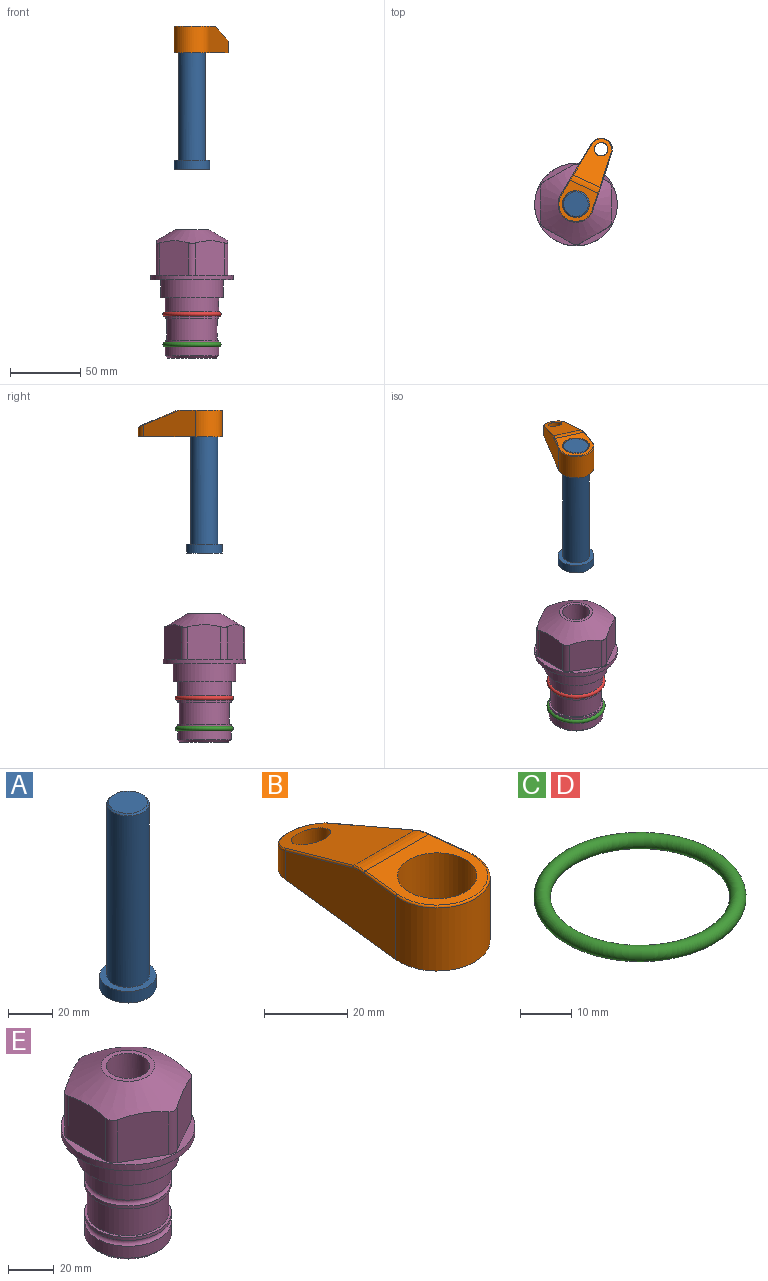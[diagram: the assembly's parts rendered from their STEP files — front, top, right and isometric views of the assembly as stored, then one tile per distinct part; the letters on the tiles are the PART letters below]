
ASSEMBLY  parts=5 mates=3
PART A: 6 faces, bbox 25.4x25.4x101.6 mm
  f0: plane 17.46x17.46mm, normal (0,0,1), area 239.5mm2, adj f5
  f1: plane 25.4x25.4mm, normal (0,0,-1), area 506.7mm2, adj f2
  f2: cylinder r=12.7mm len=25.4mm, axis (0,0,1), area 506.7mm2, adj f1,f3
  f3: plane 25.4x25.4mm, normal (0,0,1), area 221.7mm2, adj f2,f4
  f4: cylinder r=9.53mm len=94.46mm, axis (0,0,1), area 5653mm2, adj f3,f5
  f5: cone r=8.73mm half-angle=45deg, axis (0,0,-1), area 64.4mm2, adj f0,f4
PART B: 44 faces, bbox 27.5x64.5x19.1 mm
  f0: plane 2.3x0.95mm, normal (0,0,-1), area 1mm2, adj f25,f30,f34
  f1: plane 63.5x25.4mm, normal (0,0,-1), area 561.7mm2, adj f2,f3,f4,f5,f6,f7,f19,f20
  f2: cylinder r=12.7mm len=25.4mm, axis (0,0,-1), area 792.2mm2, adj f1,f3,f5,f13
  f3: plane 42.33x18.54mm, normal (0.99,0.11,0), area 647mm2, adj f1,f2,f4,f11,f12,f14
  f4: cylinder r=7.94mm len=15.78mm, axis (0,0,-1), area 158.6mm2, adj f1,f3,f5,f16
  f5: plane 42.33x18.54mm, normal (-0.99,0.11,0), area 647mm2, adj f1,f2,f4,f15,f17,f18
  f6: cylinder r=9.53mm len=19.05mm, axis (0,0,-1), area 1140.1mm2, adj f1,f8
  f7: cylinder r=4.76mm len=10.98mm, axis (0,0,-1), area 276.1mm2, adj f1,f9
  f8: plane 25.83x24.38mm, normal (0,0,1), area 262.2mm2, adj f6,f10,f11,f13,f15
  f9: plane 32.49x20.55mm, normal (0,0.34,0.94), area 489.9mm2, adj f7,f10,f14,f16,f18
  f10: cylinder r=12.7mm len=21.49mm, axis (-1,0,0), area 93.2mm2, adj f8,f9,f12,f17
  f11: cylinder r=0.51mm len=12.34mm, axis (0.11,-0.99,0), area 9.9mm2, adj f3,f8,f12,f13
  f12: bspline ~7.62x1.64mm, area 3.5mm2, adj f3,f10,f11,f14
  f13: torus R=12.19mm, axis (0,0,1), area 33.6mm2, adj f2,f8,f11,f15
  f14: cylinder r=0.51mm len=26.01mm, axis (0.1,-0.93,0.34), area 21.6mm2, adj f3,f9,f12,f16
  f15: cylinder r=0.51mm len=12.34mm, axis (0.11,0.99,0), area 9.9mm2, adj f5,f8,f13,f17
  f16: bspline ~15.78x7.05mm, area 15.7mm2, adj f4,f9,f14,f18
  f17: bspline ~7.62x1.64mm, area 3.5mm2, adj f5,f10,f15,f18
  f18: cylinder r=0.51mm len=26.01mm, axis (0.1,0.93,-0.34), area 21.6mm2, adj f5,f9,f16,f17
  f19: plane 21.6x14.29mm, normal (-0.99,-0.11,0), area 242.6mm2, adj f1,f26,f28,f34,f36,f38
  f20: plane 21.6x14.29mm, normal (0.99,-0.11,0), area 242.6mm2, adj f1,f27,f29,f37,f39,f41
  f21: cylinder r=12.7mm len=14.29mm, axis (0,0,-1), area 173.2mm2, adj f1,f26,f27,f30,f31,f33
  f22: cylinder r=7.94mm len=7.63mm, axis (0,0,-1), area 53.8mm2, adj f1,f28,f29,f42
  f23: plane 2.3x0.95mm, normal (0,0,-1), area 1mm2, adj f25,f33,f37
  f24: plane 17.94x12.32mm, normal (0,-0.34,-0.94), area 191.2mm2, adj f25,f38,f41,f42
  f25: cylinder r=9.53mm len=12.93mm, axis (-1,0,0), area 37.5mm2, adj f0,f23,f24,f31,f36,f39
  f26: cylinder r=1.59mm len=14.29mm, axis (0,0,-1), area 49mm2, adj f1,f19,f21,f32
  f27: cylinder r=1.59mm len=14.29mm, axis (0,0,-1), area 49mm2, adj f1,f20,f21,f35
  f28: cylinder r=1.59mm len=7.28mm, axis (0,0,-1), area 22.1mm2, adj f1,f19,f22,f40
  f29: cylinder r=1.59mm len=7.28mm, axis (0,0,-1), area 22.1mm2, adj f1,f20,f22,f43
  f30: torus R=14.29mm, axis (0,0,1), area 5.8mm2, adj f0,f21,f31,f32
  f31: bspline ~11.06x2.73mm, area 20.8mm2, adj f21,f25,f30,f33
  f32: sphere r=1.59mm, area 5.4mm2, adj f26,f30,f34
  f33: torus R=14.29mm, axis (0,0,1), area 5.8mm2, adj f21,f23,f31,f35
  f34: cylinder r=1.59mm len=1.68mm, axis (-0.11,0.99,0), area 2.4mm2, adj f0,f19,f32,f36
  f35: sphere r=1.59mm, area 5.4mm2, adj f27,f33,f37
  f36: bspline ~5.82x2.33mm, area 7.7mm2, adj f19,f25,f34,f38
  f37: cylinder r=1.59mm len=1.68mm, axis (0.11,0.99,0), area 2.4mm2, adj f20,f23,f35,f39
  f38: cylinder r=1.59mm len=18.33mm, axis (0.1,-0.93,0.34), area 46.7mm2, adj f19,f24,f36,f40
  f39: bspline ~5.82x2.33mm, area 7.7mm2, adj f20,f25,f37,f41
  f40: sphere r=1.59mm, area 3.6mm2, adj f28,f38,f42
  f41: cylinder r=1.59mm len=18.33mm, axis (0.1,0.93,-0.34), area 46.7mm2, adj f20,f24,f39,f43
  f42: bspline ~8.31x1.84mm, area 15.3mm2, adj f22,f24,f40,f43
  f43: sphere r=1.59mm, area 3.6mm2, adj f29,f41,f42
PART C: 1 faces, bbox 44.7x44.7x3.2 mm
  f0: torus R=19.05mm, axis (0,0,1), area 1193.9mm2
PART D: same geometry as C
PART E: 36 faces, bbox 58.7x58.7x91.2 mm
  f0: cylinder r=17.78mm len=35.56mm, axis (0,0,1), area 1670.8mm2, adj f23,f24,f31
  f1: cylinder r=19.05mm len=38.1mm, axis (0,0,1), area 1191.9mm2, adj f26,f27,f30
  f2: plane 58.66x58.66mm, normal (0,0,-1), area 1150.6mm2, adj f3,f28
  f3: cylinder r=29.33mm len=58.66mm, axis (0,0,-1), area 585.1mm2, adj f2,f4
  f4: plane 58.66x58.66mm, normal (0,0,1), area 475.9mm2, adj f3,f5,f6,f7,f8,f9,f10,f11
  f5: plane 24.5x20.32mm, normal (-0.5,0.87,0), area 562.8mm2, adj f4,f15,f16,f17
  f6: plane 24.5x20.32mm, normal (0.5,0.87,0), area 562.8mm2, adj f4,f14,f15,f17
  f7: plane 24.5x23.48mm, normal (1,0,0), area 562.8mm2, adj f4,f13,f14,f17
  f8: plane 24.5x20.32mm, normal (0.5,-0.87,0), area 562.8mm2, adj f4,f12,f13,f17
  f9: plane 24.5x20.32mm, normal (-0.5,-0.87,0), area 562.8mm2, adj f4,f11,f12,f17
  f10: plane 24.5x23.48mm, normal (-1,0,0), area 562.8mm2, adj f4,f11,f16,f17
  f11: cylinder r=5.08mm len=23.01mm, axis (0,0,-1), area 121.2mm2, adj f4,f9,f10,f17
  f12: cylinder r=5.08mm len=23.01mm, axis (0,0,-1), area 121.2mm2, adj f4,f8,f9,f17
  f13: cylinder r=5.08mm len=23.01mm, axis (0,0,-1), area 121.2mm2, adj f4,f7,f8,f17
  f14: cylinder r=5.08mm len=23.01mm, axis (0,0,-1), area 121.2mm2, adj f4,f6,f7,f17
  f15: cylinder r=5.08mm len=23.01mm, axis (0,0,-1), area 121.2mm2, adj f4,f5,f6,f17
  f16: cylinder r=5.08mm len=23.01mm, axis (0,0,-1), area 121.2mm2, adj f4,f5,f10,f17
  f17: cone r=11.73mm half-angle=60deg, axis (0,0,-1), area 2071.8mm2, adj f5,f6,f7,f8,f9,f10,f11,f12
  f18: plane 23.46x23.46mm, normal (0,0,1), area 147.4mm2, adj f17,f35
  f19: plane 34.93x34.93mm, normal (0,0,-1), area 958mm2, adj f29
  f20: cylinder r=19.05mm len=38.1mm, axis (0,0,1), area 760.1mm2, adj f21,f29
  f21: torus R=19.05mm, axis (0,0,1), area 565.3mm2, adj f20,f22
  f22: cylinder r=19.05mm len=38.1mm, axis (0,0,1), area 190mm2, adj f21,f23
  f23: plane 38.1x38.1mm, normal (0,0,1), area 146.9mm2, adj f0,f22
  f24: plane 38.1x38.1mm, normal (0,0,-1), area 146.9mm2, adj f0,f25
  f25: cylinder r=19.05mm len=38.1mm, axis (0,0,1), area 190mm2, adj f24,f26
  f26: torus R=19.05mm, axis (0,0,1), area 565.3mm2, adj f1,f25
  f27: plane 44.45x44.45mm, normal (0,0,-1), area 411.7mm2, adj f1,f28
  f28: cylinder r=22.23mm len=44.45mm, axis (0,0,1), area 1773.5mm2, adj f2,f27
  f29: cone r=19.05mm half-angle=45deg, axis (0,0,1), area 257.5mm2, adj f19,f20
  f30: cylinder r=3.17mm len=6.75mm, axis (-1,0,0), area 128mm2, adj f1,f33
  f31: cylinder r=3.17mm len=6.35mm, axis (-1,0,0), area 102.5mm2, adj f0,f33
  f32: plane 25.4x25.4mm, normal (0,0,1), area 506.7mm2, adj f33
  f33: cylinder r=12.7mm len=66.42mm, axis (0,0,-1), area 5236.2mm2, adj f30,f31,f32,f34
  f34: cone r=9.53mm half-angle=30deg, axis (0,0,-1), area 443.4mm2, adj f33,f35
  f35: cylinder r=9.53mm len=19.05mm, axis (0,0,-1), area 849mm2, adj f18,f34
PLACE A rot(axis=(0,0,1),65.4deg) t=(0,0,106.49)mm
PLACE B rot(axis=(0,0,-1),24.6deg) t=(0,0,161.1)mm
PLACE C t=(0,0,-21.59)mm
PLACE D at identity
PLACE E at identity fixed
MATE fastened C.f0 <-> E.f0  axis (0,0,1) through (0,0,-46.1)mm
MATE cylindrical A.f2 <-> E.f0  axis (0,0,1) through (0,0,132.13)mm
MATE fastened B.f2 <-> A.f2  axis (0,0,1) through (0,0,180.15)mm
